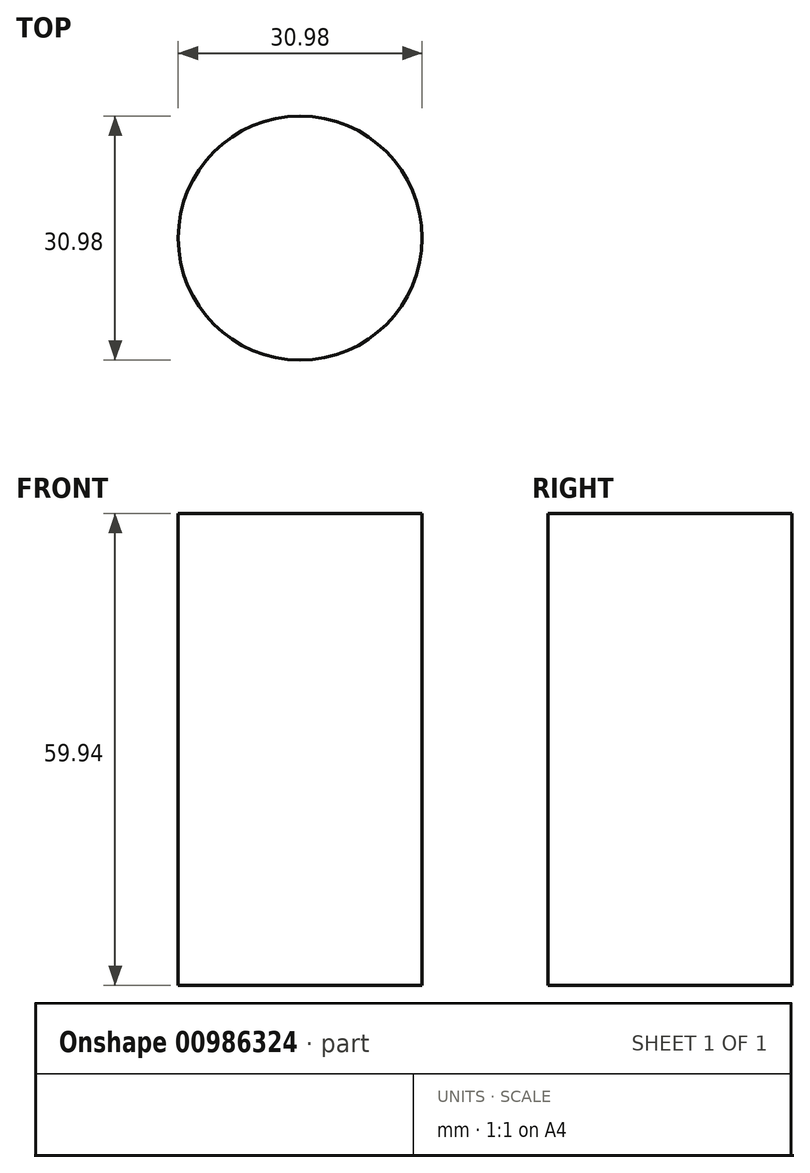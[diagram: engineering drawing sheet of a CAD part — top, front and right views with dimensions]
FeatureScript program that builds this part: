
annotation { "Feature Type Name" : "Feature", "Feature Type Description" : "" }
export const myFeature = defineFeature(function(context is Context, id is Id, definition is map)
    precondition{}
    {
        {
            var Q0;
            Q0=qCreatedBy(makeId("Top.planeOp"),FACE);
            var sketch = newSketch(context, id + "F0", { "sketchPlane" : qUnion([Q0])});
            skCircle(sketch, "E0", {"center": v(0, 0) * mm, "radius": 15.5 * mm});
            skSolve(sketch);
        }
        {
            var Q0;
            Q0=makeQuery(id+"F0.imprint","IMPRINT",FACE,{"disambiguationData":[TD([[makeQuery(id+"F0.imprint","IMPRINT",EDGE,{"derivedFrom":sQuery(id+"F0.wireOp",EDGE,"E0")}),1.0]])]});
            extrude(context, id + "F1", {"entities" : qUnion([Q0]), "endBound" : BoundingType.SYMMETRIC, "depth" : 59.94 * mm, "offsetDistance" : 25.4 * mm});
        }
    });
